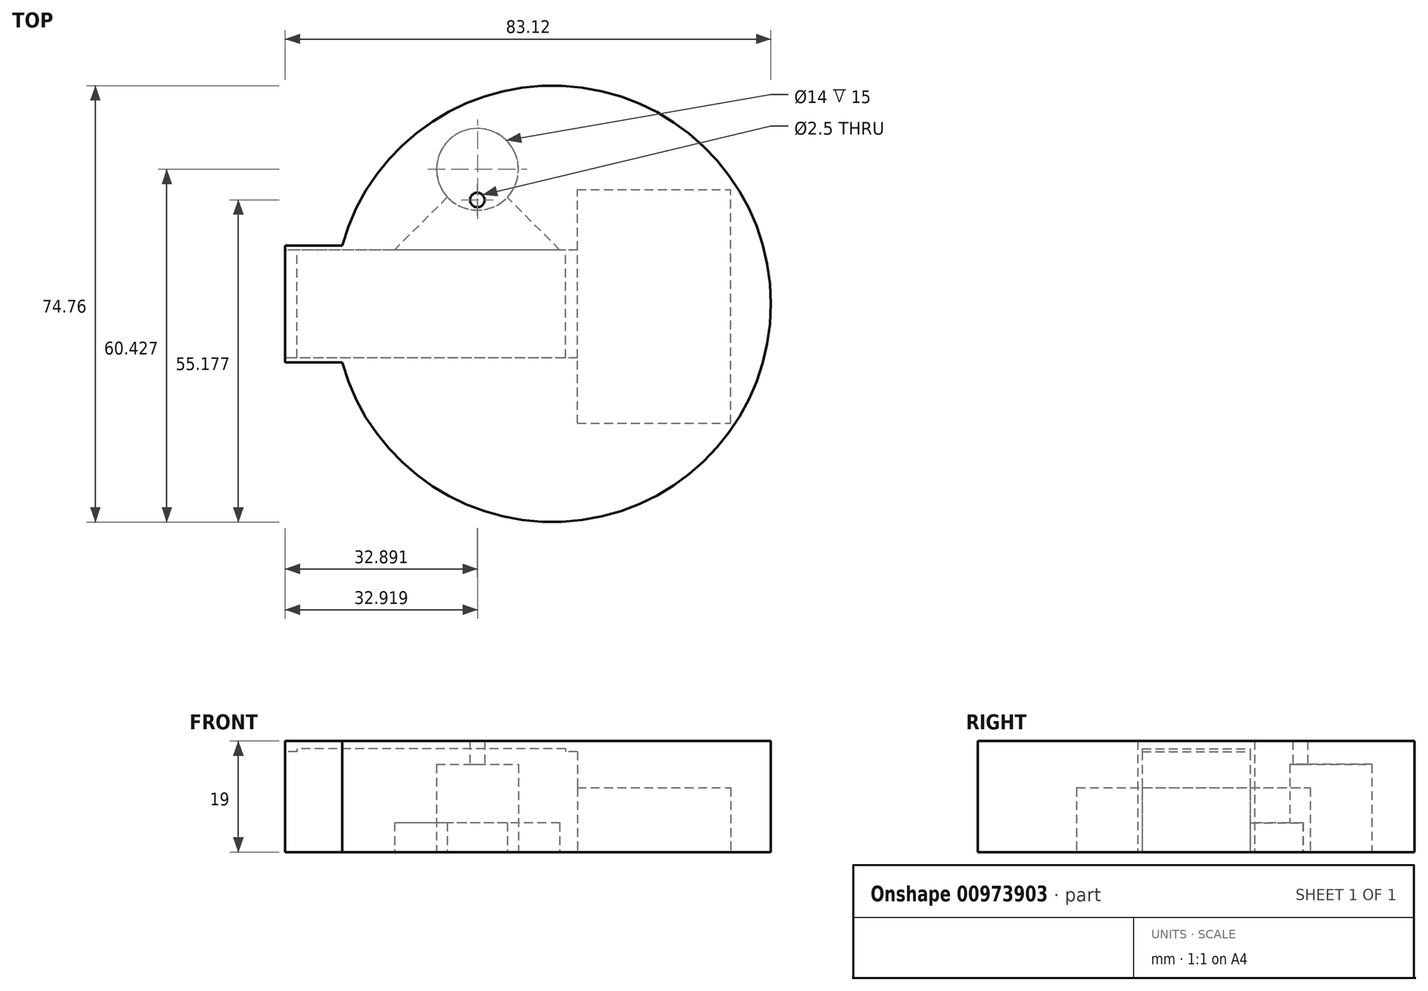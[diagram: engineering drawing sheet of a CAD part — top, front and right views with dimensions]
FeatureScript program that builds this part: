
annotation { "Feature Type Name" : "Feature", "Feature Type Description" : "" }
export const myFeature = defineFeature(function(context is Context, id is Id, definition is map)
    precondition{}
    {
        {
            var Q0;
            Q0=qCreatedBy(makeId("Top.planeOp"),FACE);
            var sketch = newSketch(context, id + "F0", { "sketchPlane" : qUnion([Q0])});
            skCircle(sketch, "E0", {"center": v(0, 0) * mm, "radius": 37.38 * mm});
            skLineSegment(sketch, "E1.bottom", {"start": v(-44.75, 10) * mm, "end": v(-30, 10) * mm});
            skLineSegment(sketch, "E1.top", {"start": v(-44.75, -10) * mm, "end": v(-30, -10) * mm});
            skLineSegment(sketch, "E1.left", {"start": v(-44.75, 10) * mm, "end": v(-44.75, -10) * mm});
            skLineSegment(sketch, "E1.right", {"start": v(-30, 10) * mm, "end": v(-30, -10) * mm});
            skPoint(sketch, "E1.middle", {"position": v(-37.38, 0) * mm});
            skLineSegment(sketch, "E2.bottom", {"start": v(-44.75, -10) * mm, "end": v(-44.75, -10) * mm});
            skLineSegment(sketch, "E2.top", {"start": v(-44.75, 10) * mm, "end": v(-44.75, 10) * mm});
            skLineSegment(sketch, "E2.left", {"start": v(-44.75, -10) * mm, "end": v(-44.75, 10) * mm});
            skLineSegment(sketch, "E2.right", {"start": v(-44.75, -10) * mm, "end": v(-44.75, 10) * mm});
            skLineSegment(sketch, "E3.bottom", {"start": v(-44.75, -10) * mm, "end": v(-45.75, -10) * mm});
            skLineSegment(sketch, "E3.top", {"start": v(-44.75, 10) * mm, "end": v(-45.75, 10) * mm});
            skLineSegment(sketch, "E3.right", {"start": v(-45.75, -10) * mm, "end": v(-45.75, 10) * mm});
            skSolve(sketch);
        }
        {
            var Q0;
            Q0 = qSketchRegion(id + "F0", true);
            extrude(context, id + "F1", {"entities" : qUnion([Q0]), "depth" : 19 * mm, "offsetDistance" : 25 * mm});
        }
        {
            var Q0;
            Q0=makeQuery(id+"F1.opExtrude","CAP_FACE",FACE,{"disambiguationData":[OSD([sQuery(id+"F0.wireOp",EDGE,"E0"),sQuery(id+"F0.wireOp",EDGE,"E1.bottom"),sQuery(id+"F0.wireOp",EDGE,"E1.top"),sQuery(id+"F0.wireOp",EDGE,"E3.bottom"),sQuery(id+"F0.wireOp",EDGE,"E3.top"),sQuery(id+"F0.wireOp",EDGE,"E3.right")])],"isStart":true});
            var sketch = newSketch(context, id + "F2", { "sketchPlane" : qUnion([Q0])});
            skLineSegment(sketch, "E4.bottom", {"start": v(4.25, 9.25) * mm, "end": v(-45.75, 9.25) * mm});
            skLineSegment(sketch, "E4.top", {"start": v(4.25, -9.25) * mm, "end": v(-45.75, -9.25) * mm});
            skLineSegment(sketch, "E4.left", {"start": v(4.25, 9.25) * mm, "end": v(4.25, -9.25) * mm});
            skLineSegment(sketch, "E4.right", {"start": v(-45.75, 9.25) * mm, "end": v(-45.75, -9.25) * mm});
            skPoint(sketch, "E4.middle", {"position": v(-20.75, 0) * mm});
            skPoint(sketch, "E5", {"position": v(-44.75, 0) * mm});
            skSolve(sketch);
        }
        {
            var Q0;
            Q0 = qSketchRegion(id + "F2", true);
            extrude(context, id + "F3", {"entities" : qUnion([Q0]), "operationType" : NewBodyOperationType.REMOVE, "oppositeDirection" : true, "depth" : 17.2 * mm, "offsetDistance" : 25 * mm});
        }
        {
            var Q0;
            Q0=makeQuery(id+"F3.boolean.opBoolean","COPY",FACE,{"derivedFrom":makeQuery(id+"F3.opExtrude","CAP_FACE",FACE,{"disambiguationData":[OSD([sQuery(id+"F2.wireOp",EDGE,"E4.bottom"),sQuery(id+"F2.wireOp",EDGE,"E4.top"),sQuery(id+"F2.wireOp",EDGE,"E4.left"),sQuery(id+"F2.wireOp",EDGE,"E4.right")])],"isStart":false})});
            var sketch = newSketch(context, id + "F4", { "sketchPlane" : qUnion([Q0])});
            skLineSegment(sketch, "E6.bottom", {"start": v(-43.75, 9.25) * mm, "end": v(2.25, 9.25) * mm});
            skLineSegment(sketch, "E6.top", {"start": v(-43.75, -9.25) * mm, "end": v(2.25, -9.25) * mm});
            skLineSegment(sketch, "E6.left", {"start": v(-43.75, 9.25) * mm, "end": v(-43.75, -9.25) * mm});
            skLineSegment(sketch, "E6.right", {"start": v(2.25, 9.25) * mm, "end": v(2.25, -9.25) * mm});
            skSolve(sketch);
        }
        {
            var Q0;
            Q0 = qSketchRegion(id + "F4", true);
            extrude(context, id + "F5", {"entities" : qUnion([Q0]), "operationType" : NewBodyOperationType.REMOVE, "oppositeDirection" : true, "depth" : .5 * mm, "offsetDistance" : 25 * mm});
        }
        {
            var Q0;
            Q0=makeQuery(id+"F1.opExtrude","CAP_FACE",FACE,{"disambiguationData":[OSD([sQuery(id+"F0.wireOp",EDGE,"E0"),sQuery(id+"F0.wireOp",EDGE,"E1.bottom"),sQuery(id+"F0.wireOp",EDGE,"E1.top"),sQuery(id+"F0.wireOp",EDGE,"E1.left")])],"isStart":true});
            var sketch = newSketch(context, id + "F6", { "sketchPlane" : qUnion([Q0])});
            skLineSegment(sketch, "E7.bottom", {"start": v(4.25, 20.46) * mm, "end": v(30.5, 20.46) * mm});
            skLineSegment(sketch, "E7.top", {"start": v(4.25, -19.54) * mm, "end": v(30.5, -19.54) * mm});
            skLineSegment(sketch, "E7.left", {"start": v(4.25, 20.46) * mm, "end": v(4.25, -19.54) * mm});
            skLineSegment(sketch, "E7.right", {"start": v(30.5, 20.46) * mm, "end": v(30.5, -19.54) * mm});
            skSolve(sketch);
        }
        {
            var Q0;
            {var subQ3=sQuery(id+"F6.wireOp",EDGE,"E7.bottom");Q0=makeQuery(id+"F6.imprint","IMPRINT",FACE,{"disambiguationData":[TD([[makeQuery(id+"F6.imprint","IMPRINT",EDGE,{"derivedFrom":subQ3}),-1.0]])]});}
            extrude(context, id + "F7", {"entities" : qUnion([Q0]), "operationType" : NewBodyOperationType.REMOVE, "oppositeDirection" : true, "depth" : 11 * mm, "offsetDistance" : 25 * mm});
        }
        {
            var Q0;
            Q0=makeQuery(id+"F1.opExtrude","CAP_FACE",FACE,{"disambiguationData":[OSD([sQuery(id+"F0.wireOp",EDGE,"E0"),sQuery(id+"F0.wireOp",EDGE,"E1.bottom"),sQuery(id+"F0.wireOp",EDGE,"E1.top"),sQuery(id+"F0.wireOp",EDGE,"E3.bottom"),sQuery(id+"F0.wireOp",EDGE,"E3.top"),sQuery(id+"F0.wireOp",EDGE,"E3.right")])],"isStart":true});
            var sketch = newSketch(context, id + "F8", { "sketchPlane" : qUnion([Q0])});
            skCircle(sketch, "E8", {"center": v(-12.83, -23.05) * mm, "radius": 7 * mm});
            skSolve(sketch);
        }
        {
            var Q0;
            Q0=makeQuery(id+"F8.imprint","IMPRINT",FACE,{"disambiguationData":[TD([[makeQuery(id+"F8.imprint","IMPRINT",EDGE,{"derivedFrom":sQuery(id+"F8.wireOp",EDGE,"E8")}),-1.0]])]});
            var sketch = newSketch(context, id + "F9", { "sketchPlane" : qUnion([Q0])});
            skLineSegment(sketch, "E9", {"start": v(-12.9, -23.4) * mm, "end": v(-27.03, -9.25) * mm});
            skLineSegment(sketch, "E10", {"start": v(-27.03, -9.25) * mm, "end": v(1.25, -9.25) * mm});
            skLineSegment(sketch, "E11", {"start": v(1.25, -9.25) * mm, "end": v(-12.9, -23.4) * mm});
            skSolve(sketch);
        }
        {
            var Q0;
            Q0 = qSketchRegion(id + "F9", true);
            extrude(context, id + "F10", {"entities" : qUnion([Q0]), "operationType" : NewBodyOperationType.REMOVE, "oppositeDirection" : true, "depth" : 5 * mm, "offsetDistance" : 25 * mm});
        }
        {
            var Q0;
            Q0=makeQuery(id+"F8.imprint","IMPRINT",FACE,{"disambiguationData":[TD([[makeQuery(id+"F8.imprint","IMPRINT",EDGE,{"derivedFrom":sQuery(id+"F8.wireOp",EDGE,"E8")}),1.0]])]});
            extrude(context, id + "F11", {"entities" : qUnion([Q0]), "operationType" : NewBodyOperationType.REMOVE, "oppositeDirection" : true, "depth" : 15 * mm, "offsetDistance" : 25 * mm});
        }
        {
            var Q0;
            Q0=makeQuery(id+"F11.boolean.opBoolean","COPY",FACE,{"derivedFrom":makeQuery(id+"F11.opExtrude","CAP_FACE",FACE,{"disambiguationData":[OSD([sQuery(id+"F8.wireOp",EDGE,"E8")])],"isStart":false})});
            var sketch = newSketch(context, id + "F12", { "sketchPlane" : qUnion([Q0])});
            skCircle(sketch, "E12", {"center": v(-12.86, -17.8) * mm, "radius": 1.25 * mm});
            skSolve(sketch);
        }
        {
            var Q0;
            Q0=makeQuery(id+"F12.imprint","IMPRINT",FACE,{"disambiguationData":[TD([[makeQuery(id+"F12.imprint","IMPRINT",EDGE,{"derivedFrom":sQuery(id+"F12.wireOp",EDGE,"E12")}),1.0]])]});
            extrude(context, id + "F13", {"entities" : qUnion([Q0]), "operationType" : NewBodyOperationType.REMOVE, "oppositeDirection" : true, "depth" : 4 * mm, "offsetDistance" : 25 * mm});
        }
    });
